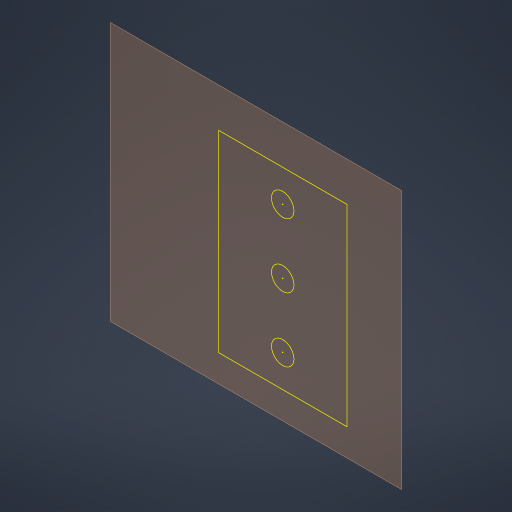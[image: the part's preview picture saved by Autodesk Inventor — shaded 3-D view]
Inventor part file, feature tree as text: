
AUTODESK INVENTOR PART (.ipt)
format: ipt  version: 2023 (Build 270158000, 158)  size: 159,232 bytes
history: native  units: mm
features: other x3, plane x1, sketch x1, reference x1
ambient origin geometry x8: Origin, YZ Plane, XZ Plane, XY Plane, X Axis, Y Axis, Z Axis, Center Point
feature tree (6):
  plane  "Work Plane1"
  sketch  "Sketch1"
  reference  "Reference1"
  parser-record x1  (decoder bookkeeping rows leaked as tree rows — omitted from the tree; the rows remain in map.json)
  other  "_arm.iam"
  other  "body holder:1"
note: 1 file-system path scrubbed to <path> (originals preserved in map.json)
